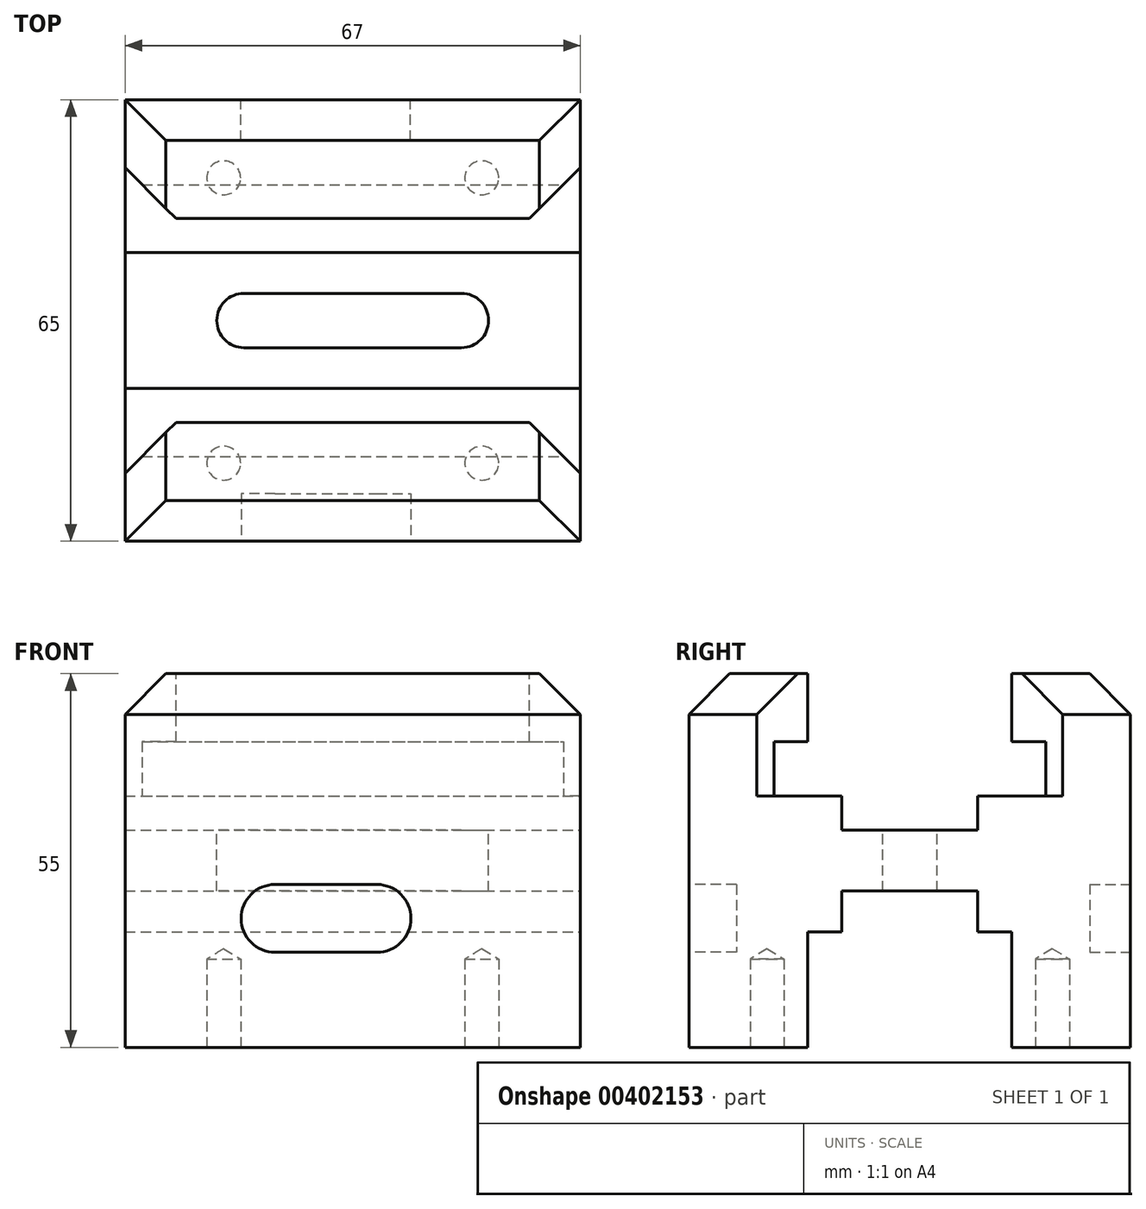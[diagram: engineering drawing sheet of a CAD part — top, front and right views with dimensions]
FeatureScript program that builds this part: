
annotation { "Feature Type Name" : "Feature", "Feature Type Description" : "" }
export const myFeature = defineFeature(function(context is Context, id is Id, definition is map)
    precondition{}
    {
        {
            var Q0;
            Q0=qCreatedBy(makeId("Front.planeOp"),FACE);
            var sketch = newSketch(context, id + "F0", { "sketchPlane" : qUnion([Q0])});
            skLineSegment(sketch, "E0.bottom", {"start": v(33.5, 27.5) * mm, "end": v(-33.5, 27.5) * mm});
            skLineSegment(sketch, "E0.top", {"start": v(33.5, -27.5) * mm, "end": v(-33.5, -27.5) * mm});
            skLineSegment(sketch, "E0.left", {"start": v(33.5, 27.5) * mm, "end": v(33.5, -27.5) * mm});
            skLineSegment(sketch, "E0.right", {"start": v(-33.5, 27.5) * mm, "end": v(-33.5, -27.5) * mm});
            skPoint(sketch, "E0.middle", {"position": v(0, 0) * mm});
            skSolve(sketch);
        }
        {
            var Q0;
            Q0=makeQuery(id+"F0.imprint","IMPRINT",FACE,{"disambiguationData":[TD([[makeQuery(id+"F0.imprint","IMPRINT",EDGE,{"derivedFrom":sQuery(id+"F0.wireOp",EDGE,"E0.bottom")}),1.0]])]});
            extrude(context, id + "F1", {"entities" : qUnion([Q0]), "depth" : 65 * mm, "symmetric" : true});
        }
        {
            var Q0;
            Q0=qCreatedBy(makeId("Right.planeOp"),FACE);
            var sketch = newSketch(context, id + "F2", { "sketchPlane" : qUnion([Q0])});
            skLineSegment(sketch, "E1", {"start": v(0, 0) * mm, "end": v(0, 27.5) * mm});
            skLineSegment(sketch, "E2", {"start": v(0, 27.5) * mm, "end": v(15, 27.5) * mm});
            skLineSegment(sketch, "E3", {"start": v(15, 27.5) * mm, "end": v(15, 17.5) * mm});
            skLineSegment(sketch, "E4", {"start": v(15, 17.5) * mm, "end": v(20, 17.5) * mm});
            skLineSegment(sketch, "E5", {"start": v(20, 17.5) * mm, "end": v(20, 9.5) * mm});
            skLineSegment(sketch, "E6", {"start": v(20, 9.5) * mm, "end": v(10, 9.5) * mm});
            skLineSegment(sketch, "E7", {"start": v(10, 9.5) * mm, "end": v(10, 4.5) * mm});
            skLineSegment(sketch, "E8", {"start": v(10, 4.5) * mm, "end": v(0, 4.5) * mm});
            skLineSegment(sketch, "E9.MirrorCS", {"start": v(-10, 9.5) * mm, "end": v(-10, 4.5) * mm});
            skLineSegment(sketch, "E10.MirrorCS", {"start": v(-20, 9.5) * mm, "end": v(-10, 9.5) * mm});
            skLineSegment(sketch, "E11.MirrorCS", {"start": v(-20, 17.5) * mm, "end": v(-20, 9.5) * mm});
            skLineSegment(sketch, "E12.MirrorCS", {"start": v(-10, 4.5) * mm, "end": v(0, 4.5) * mm});
            skLineSegment(sketch, "E13.MirrorCS", {"start": v(0, 27.5) * mm, "end": v(-15, 27.5) * mm});
            skLineSegment(sketch, "E14.MirrorCS", {"start": v(-15, 27.5) * mm, "end": v(-15, 17.5) * mm});
            skLineSegment(sketch, "E15.MirrorCS", {"start": v(-15, 17.5) * mm, "end": v(-20, 17.5) * mm});
            skLineSegment(sketch, "E16", {"start": v(0, 0) * mm, "end": v(0, -27.5) * mm});
            skLineSegment(sketch, "E17", {"start": v(0, -27.5) * mm, "end": v(15, -27.5) * mm});
            skLineSegment(sketch, "E18", {"start": v(15, -27.5) * mm, "end": v(15, -10.5) * mm});
            skLineSegment(sketch, "E19", {"start": v(15, -10.5) * mm, "end": v(10, -10.5) * mm});
            skLineSegment(sketch, "E20", {"start": v(10, -10.5) * mm, "end": v(10, -4.5) * mm});
            skLineSegment(sketch, "E21", {"start": v(10, -4.5) * mm, "end": v(0, -4.5) * mm});
            skLineSegment(sketch, "E22.MirrorCS", {"start": v(-10, -10.5) * mm, "end": v(-10, -4.5) * mm});
            skLineSegment(sketch, "E23.MirrorCS", {"start": v(-15, -27.5) * mm, "end": v(-15, -10.5) * mm});
            skLineSegment(sketch, "E24.MirrorCS", {"start": v(-10, -4.5) * mm, "end": v(0, -4.5) * mm});
            skLineSegment(sketch, "E25.MirrorCS", {"start": v(0, -27.5) * mm, "end": v(-15, -27.5) * mm});
            skLineSegment(sketch, "E26.MirrorCS", {"start": v(-15, -10.5) * mm, "end": v(-10, -10.5) * mm});
            skSolve(sketch);
        }
        {
            var Q0;
            Q0=makeQuery(id+"F2.imprint","IMPRINT",FACE,{"disambiguationData":[TD([[makeQuery(id+"F2.imprint","IMPRINT",EDGE,{"derivedFrom":sQuery(id+"F2.wireOp",EDGE,"E9.MirrorCS")}),1.0]])]});
            var Q1;
            {var subQ0=sQuery(id+"F2.wireOp",EDGE,"E2");Q1=makeQuery(id+"F2.imprint","IMPRINT",FACE,{"disambiguationData":[TD([[makeQuery(id+"F2.imprint","IMPRINT",EDGE,{"derivedFrom":subQ0}),-1.0]])]});}
            var Q2;
            {var subQ0=sQuery(id+"F2.wireOp",EDGE,"E17");Q2=makeQuery(id+"F2.imprint","IMPRINT",FACE,{"disambiguationData":[TD([[makeQuery(id+"F2.imprint","IMPRINT",EDGE,{"derivedFrom":subQ0}),1.0]])]});}
            var Q3;
            Q3=makeQuery(id+"F2.imprint","IMPRINT",FACE,{"disambiguationData":[TD([[makeQuery(id+"F2.imprint","IMPRINT",EDGE,{"derivedFrom":sQuery(id+"F2.wireOp",EDGE,"E22.MirrorCS")}),-1.0]])]});
            extrude(context, id + "F3", {"entities" : qUnion([Q0, Q1, Q2, Q3]), "operationType" : NewBodyOperationType.REMOVE, "oppositeDirection" : true, "depth" : 67 * mm, "symmetric" : true});
        }
        {
            var Q0;
            Q0=qCreatedBy(makeId("Top.planeOp"),FACE);
            var sketch = newSketch(context, id + "F4", { "sketchPlane" : qUnion([Q0])});
            skLineSegment(sketch, "E27.bottom", {"start": v(16, 4) * mm, "end": v(-16, 4) * mm});
            skLineSegment(sketch, "E27.top", {"start": v(16, -4) * mm, "end": v(-16, -4) * mm});
            skLineSegment(sketch, "E27.left", {"start": v(20, 0) * mm, "end": v(20, 0) * mm});
            skLineSegment(sketch, "E27.right", {"start": v(-20, 0) * mm, "end": v(-20, 0) * mm});
            skPoint(sketch, "E27.middle", {"position": v(0, 0) * mm});
            skPoint(sketch, "E28.visualSharp", {"position": v(20, -4) * mm});
            skArc(sketch, "E28.filletArc", {"start": v(16, -4) * mm, "mid": v(18.83, -2.83) * mm, "end": v(20, 0) * mm});
            skPoint(sketch, "E29.visualSharp", {"position": v(20, 4) * mm});
            skArc(sketch, "E29.filletArc", {"start": v(20, 0) * mm, "mid": v(18.83, 2.83) * mm, "end": v(16, 4) * mm});
            skPoint(sketch, "E30.visualSharp", {"position": v(-20, 4) * mm});
            skArc(sketch, "E30.filletArc", {"start": v(-16, 4) * mm, "mid": v(-18.83, 2.83) * mm, "end": v(-20, 0) * mm});
            skPoint(sketch, "E31.visualSharp", {"position": v(-20, -4) * mm});
            skArc(sketch, "E31.filletArc", {"start": v(-20, 0) * mm, "mid": v(-18.83, -2.83) * mm, "end": v(-16, -4) * mm});
            skSolve(sketch);
        }
        {
            var Q0;
            Q0=makeQuery(id+"F4.imprint","IMPRINT",FACE,{"disambiguationData":[TD([[makeQuery(id+"F4.imprint","IMPRINT",EDGE,{"derivedFrom":sQuery(id+"F4.wireOp",EDGE,"E27.bottom")}),1.0]])]});
            extrude(context, id + "F5", {"entities" : qUnion([Q0]), "operationType" : NewBodyOperationType.REMOVE, "oppositeDirection" : true, "depth" : (55 - 23 - 23) * mm, "symmetric" : true});
        }
        {
            var Q0;
            Q0=makeQuery(id+"F1.opExtrude","CAP_FACE",FACE,{"disambiguationData":[OSD([sQuery(id+"F0.wireOp",EDGE,"E0.bottom"),sQuery(id+"F0.wireOp",EDGE,"E0.top"),sQuery(id+"F0.wireOp",EDGE,"E0.left"),sQuery(id+"F0.wireOp",EDGE,"E0.right")])],"isStart":false});
            var sketch = newSketch(context, id + "F6", { "sketchPlane" : qUnion([Q0])});
            skLineSegment(sketch, "E32", {"start": v(0, 0) * mm, "end": v(0, -8.5) * mm});
            skPoint(sketch, "E32.endSnap0", {"position": v(0, -27.5) * mm});
            skLineSegment(sketch, "E33", {"start": v(0, -8.5) * mm, "end": v(-4, -8.5) * mm});
            skLineSegment(sketch, "E34.bottom", {"start": v(-11.43, -3.52) * mm, "end": v(3.57, -3.52) * mm});
            skLineSegment(sketch, "E34.top", {"start": v(-11.43, -13.52) * mm, "end": v(3.57, -13.52) * mm});
            skLineSegment(sketch, "E34.left", {"start": v(-16.43, -8.52) * mm, "end": v(-16.43, -8.52) * mm});
            skLineSegment(sketch, "E34.right", {"start": v(8.57, -8.52) * mm, "end": v(8.57, -8.52) * mm});
            skPoint(sketch, "E34.middle", {"position": v(-3.93, -8.52) * mm});
            skPoint(sketch, "E35.visualSharp", {"position": v(-16.43, -13.52) * mm});
            skArc(sketch, "E35.filletArc", {"start": v(-16.43, -8.52) * mm, "mid": v(-14.96, -12.06) * mm, "end": v(-11.43, -13.52) * mm});
            skPoint(sketch, "E36.visualSharp", {"position": v(-16.43, -3.52) * mm});
            skArc(sketch, "E36.filletArc", {"start": v(-11.43, -3.52) * mm, "mid": v(-14.96, -4.99) * mm, "end": v(-16.43, -8.52) * mm});
            skPoint(sketch, "E37.visualSharp", {"position": v(8.57, -3.52) * mm});
            skArc(sketch, "E37.filletArc", {"start": v(8.57, -8.52) * mm, "mid": v(7.1, -4.99) * mm, "end": v(3.57, -3.52) * mm});
            skPoint(sketch, "E38.visualSharp", {"position": v(8.57, -13.52) * mm});
            skArc(sketch, "E38.filletArc", {"start": v(3.57, -13.52) * mm, "mid": v(7.1, -12.06) * mm, "end": v(8.57, -8.52) * mm});
            skSolve(sketch);
        }
        {
            var Q0;
            Q0=makeQuery(id+"F1.opExtrude","CAP_FACE",FACE,{"disambiguationData":[OSD([sQuery(id+"F0.wireOp",EDGE,"E0.bottom"),sQuery(id+"F0.wireOp",EDGE,"E0.top"),sQuery(id+"F0.wireOp",EDGE,"E0.left"),sQuery(id+"F0.wireOp",EDGE,"E0.right")])],"isStart":true});
            var sketch = newSketch(context, id + "F7", { "sketchPlane" : qUnion([Q0])});
            skLineSegment(sketch, "E39", {"start": v(0, 0) * mm, "end": v(0, -8.5) * mm});
            skLineSegment(sketch, "E40", {"start": v(0, -8.5) * mm, "end": v(4, -8.5) * mm});
            skLineSegment(sketch, "E41.bottom", {"start": v(-3.5, -3.5) * mm, "end": v(11.5, -3.5) * mm});
            skLineSegment(sketch, "E41.top", {"start": v(-3.5, -13.5) * mm, "end": v(11.5, -13.5) * mm});
            skLineSegment(sketch, "E41.left", {"start": v(-8.5, -8.5) * mm, "end": v(-8.5, -8.5) * mm});
            skLineSegment(sketch, "E41.right", {"start": v(16.5, -8.5) * mm, "end": v(16.5, -8.5) * mm});
            skPoint(sketch, "E41.middle", {"position": v(4, -8.5) * mm});
            skPoint(sketch, "E42.visualSharp", {"position": v(-8.5, -3.5) * mm});
            skArc(sketch, "E42.filletArc", {"start": v(-3.5, -3.5) * mm, "mid": v(-7.04, -4.96) * mm, "end": v(-8.5, -8.5) * mm});
            skPoint(sketch, "E43.visualSharp", {"position": v(-8.5, -13.5) * mm});
            skArc(sketch, "E43.filletArc", {"start": v(-8.5, -8.5) * mm, "mid": v(-7.04, -12.04) * mm, "end": v(-3.5, -13.5) * mm});
            skPoint(sketch, "E44.visualSharp", {"position": v(16.5, -13.5) * mm});
            skArc(sketch, "E44.filletArc", {"start": v(11.5, -13.5) * mm, "mid": v(15.04, -12.04) * mm, "end": v(16.5, -8.5) * mm});
            skPoint(sketch, "E45.visualSharp", {"position": v(16.5, -3.5) * mm});
            skArc(sketch, "E45.filletArc", {"start": v(16.5, -8.5) * mm, "mid": v(15.04, -4.96) * mm, "end": v(11.5, -3.5) * mm});
            skSolve(sketch);
        }
        {
            var Q0;
            Q0=makeQuery(id+"F7.imprint","IMPRINT",FACE,{"disambiguationData":[TD([[makeQuery(id+"F7.imprint","IMPRINT",EDGE,{"derivedFrom":sQuery(id+"F7.wireOp",EDGE,"E41.top")}),1.0]])]});
            extrude(context, id + "F8", {"entities" : qUnion([Q0]), "operationType" : NewBodyOperationType.REMOVE, "oppositeDirection" : true, "depth" : 6 * mm});
        }
        {
            var Q0;
            Q0=makeQuery(id+"F6.imprint","IMPRINT",FACE,{"disambiguationData":[TD([[makeQuery(id+"F6.imprint","IMPRINT",EDGE,{"derivedFrom":sQuery(id+"F6.wireOp",EDGE,"E34.top")}),1.0]])]});
            extrude(context, id + "F9", {"entities" : qUnion([Q0]), "operationType" : NewBodyOperationType.REMOVE, "oppositeDirection" : true, "depth" : 7 * mm});
        }
        {
            var Q0;
            {var subQ2=sQuery(id+"F0.wireOp",EDGE,"E0.top");Q0=makeQuery(id+"F3.boolean.opBoolean","SPLIT",FACE,{"disambiguationData":[TD([makeQuery(id+"F3.opExtrude","SWEPT_FACE",FACE,{"disambiguationData":[OSD([sQuery(id+"F2.wireOp",EDGE,"E23.MirrorCS")])]})])],"derivedFrom":makeQuery(id+"F1.opExtrude","SWEPT_FACE",FACE,{"disambiguationData":[OSD([subQ2])]})});}
            var sketch = newSketch(context, id + "F10", { "sketchPlane" : qUnion([Q0])});
            skLineSegment(sketch, "E46.bottom", {"start": v(-19, 21) * mm, "end": v(19, 21) * mm});
            skLineSegment(sketch, "E46.top", {"start": v(-19, -21) * mm, "end": v(19, -21) * mm});
            skLineSegment(sketch, "E46.left", {"start": v(-19, 21) * mm, "end": v(-19, -21) * mm});
            skLineSegment(sketch, "E46.right", {"start": v(19, 21) * mm, "end": v(19, -21) * mm});
            skPoint(sketch, "E46.middle", {"position": v(0, 0) * mm});
            skCircle(sketch, "E47", {"center": v(-19, 21) * mm, "radius": 2.5 * mm});
            skCircle(sketch, "E48", {"center": v(19, 21) * mm, "radius": 2.5 * mm});
            skCircle(sketch, "E49", {"center": v(19, -21) * mm, "radius": 2.5 * mm});
            skCircle(sketch, "E50", {"center": v(-19, -21) * mm, "radius": 2.5 * mm});
            skSolve(sketch);
        }
        {
            var Q0;
            Q0=sQuery(id+"F10.wireOp",VERTEX,"E46.left.end");
            var Q1;
            Q1=sQuery(id+"F10.wireOp",VERTEX,"E47.center");
            var Q2;
            Q2=sQuery(id+"F10.wireOp",VERTEX,"E46.right.start");
            var Q3;
            Q3=sQuery(id+"F10.wireOp",VERTEX,"E46.right.end");
            var Q4;
            Q4=makeQuery(id+"F1.opExtrude","SWEPT_BODY",BODY,{"disambiguationData":[OSD([sQuery(id+"F0.wireOp",EDGE,"E0.bottom"),sQuery(id+"F0.wireOp",EDGE,"E0.top"),sQuery(id+"F0.wireOp",EDGE,"E0.left"),sQuery(id+"F0.wireOp",EDGE,"E0.right")])]});
            hole(context, id + "F11", {"style" : HoleStyle.SIMPLE, "endStyle" : HoleEndStyle.BLIND, "standardTappedOrClearance" : lookupTablePath({ "standard" : "ISO", "engagement" : "75%", "pitch" : "1 mm", "size" : "M6", "type" : "Tapped" }), "standardBlindInLast" : lookupTablePath({ "standard" : "ISO", "engagement" : "75%", "pitch" : "1 mm", "size" : "M6", "type" : "Tapped" }), "holeDiameter" : 5 * mm, "showTappedDepth" : true, "holeDepth" : 13 * mm, "isTappedThrough" : true, "tappedDepth" : 10 * mm, "tapClearance" : 3, "locations" : qUnion([Q0, Q1, Q2, Q3]), "scope" : qUnion([Q4]), "majorDiameter" : 6 * mm});
        }
        {
            var Q0;
            {var subQ2=sQuery(id+"F0.wireOp",EDGE,"E0.bottom");Q0=makeQuery(id+"F3.boolean.opBoolean","SPLIT",FACE,{"disambiguationData":[TD([makeQuery(id+"F3.opExtrude","SWEPT_FACE",FACE,{"disambiguationData":[OSD([sQuery(id+"F2.wireOp",EDGE,"E3")])]})])],"derivedFrom":makeQuery(id+"F1.opExtrude","SWEPT_FACE",FACE,{"disambiguationData":[OSD([subQ2])]})});}
            var sketch = newSketch(context, id + "F12", { "sketchPlane" : qUnion([Q0])});
            skLineSegment(sketch, "E51", {"start": v(0, 0) * mm, "end": v(0, 15) * mm});
            skLineSegment(sketch, "E52", {"start": v(0, 15) * mm, "end": v(-26, 15) * mm});
            skLineSegment(sketch, "E53", {"start": v(-33.5, 15) * mm, "end": v(-33.5, 22.5) * mm});
            skLineSegment(sketch, "E54", {"start": v(-33.5, 22.5) * mm, "end": v(-26, 15) * mm});
            skLineSegment(sketch, "E55", {"start": v(0, 0) * mm, "end": v(-39.07, 0) * mm});
            skLineSegment(sketch, "E56", {"start": v(0, 15) * mm, "end": v(0, 24.8) * mm});
            skLineSegment(sketch, "E57", {"start": v(-26, 15) * mm, "end": v(-33.5, 15) * mm});
            skLineSegment(sketch, "E58.MirrorCS", {"start": v(33.5, 22.5) * mm, "end": v(26, 15) * mm});
            skLineSegment(sketch, "E59.MirrorCS", {"start": v(33.5, 15) * mm, "end": v(33.5, 22.5) * mm});
            skLineSegment(sketch, "E60.MirrorCS", {"start": v(26, 15) * mm, "end": v(33.5, 15) * mm});
            skLineSegment(sketch, "E61.MirrorCS", {"start": v(33.5, -22.5) * mm, "end": v(26, -15) * mm});
            skLineSegment(sketch, "E62.MirrorCS", {"start": v(33.5, -15) * mm, "end": v(33.5, -22.5) * mm});
            skLineSegment(sketch, "E63.MirrorCS", {"start": v(26, -15) * mm, "end": v(33.5, -15) * mm});
            skLineSegment(sketch, "E64.MirrorCS", {"start": v(-33.5, -22.5) * mm, "end": v(-26, -15) * mm});
            skLineSegment(sketch, "E65.MirrorCS", {"start": v(0, -15) * mm, "end": v(-26, -15) * mm});
            skLineSegment(sketch, "E66.MirrorCS", {"start": v(-33.5, -15) * mm, "end": v(-33.5, -22.5) * mm});
            skLineSegment(sketch, "E67.MirrorCS", {"start": v(-26, -15) * mm, "end": v(-33.5, -15) * mm});
            skSolve(sketch);
        }
        {
            var Q0;
            Q0=makeQuery(id+"F12.imprint","IMPRINT",FACE,{"disambiguationData":[TD([[makeQuery(id+"F12.imprint","IMPRINT",EDGE,{"derivedFrom":sQuery(id+"F12.wireOp",EDGE,"E53")}),-1.0]])]});
            var Q1;
            Q1=makeQuery(id+"F12.imprint","IMPRINT",FACE,{"disambiguationData":[TD([[makeQuery(id+"F12.imprint","IMPRINT",EDGE,{"derivedFrom":sQuery(id+"F12.wireOp",EDGE,"E60.MirrorCS")}),1.0]])]});
            var Q2;
            Q2=makeQuery(id+"F12.imprint","IMPRINT",FACE,{"disambiguationData":[TD([[makeQuery(id+"F12.imprint","IMPRINT",EDGE,{"derivedFrom":sQuery(id+"F12.wireOp",EDGE,"E62.MirrorCS")}),-1.0]])]});
            var Q3;
            Q3=makeQuery(id+"F12.imprint","IMPRINT",FACE,{"disambiguationData":[TD([[makeQuery(id+"F12.imprint","IMPRINT",EDGE,{"derivedFrom":sQuery(id+"F12.wireOp",EDGE,"E64.MirrorCS")}),1.0]])]});
            extrude(context, id + "F13", {"entities" : qUnion([Q0, Q1, Q2, Q3]), "operationType" : NewBodyOperationType.REMOVE, "oppositeDirection" : true, "depth" : 18 * mm});
        }
        {
            var Q0;
            {var subQ0=sQuery(id+"F0.wireOp",EDGE,"E0.bottom");var subQ1=sQuery(id+"F0.wireOp",EDGE,"E0.left");Q0=makeQuery(id+"F3.boolean.opBoolean","SPLIT",EDGE,{"disambiguationData":[TD([makeQuery(id+"F3.opExtrude","SWEPT_FACE",FACE,{"disambiguationData":[OSD([sQuery(id+"F2.wireOp",EDGE,"E14.MirrorCS")])]})])],"derivedFrom":makeQuery(id+"F1.opExtrude","SWEPT_EDGE",EDGE,{"disambiguationData":[OSD([subQ0,subQ1])]})});}
            var Q1;
            Q1=makeQuery(id+"F1.opExtrude","CAP_EDGE",EDGE,{"disambiguationData":[OSD([sQuery(id+"F0.wireOp",EDGE,"E0.bottom")])],"isStart":false});
            var Q2;
            {var subQ0=sQuery(id+"F0.wireOp",EDGE,"E0.bottom");var subQ1=sQuery(id+"F0.wireOp",EDGE,"E0.right");Q2=makeQuery(id+"F3.boolean.opBoolean","SPLIT",EDGE,{"disambiguationData":[TD([makeQuery(id+"F3.opExtrude","SWEPT_FACE",FACE,{"disambiguationData":[OSD([sQuery(id+"F2.wireOp",EDGE,"E14.MirrorCS")])]})])],"derivedFrom":makeQuery(id+"F1.opExtrude","SWEPT_EDGE",EDGE,{"disambiguationData":[OSD([subQ0,subQ1])]})});}
            var Q3;
            {var subQ0=sQuery(id+"F0.wireOp",EDGE,"E0.bottom");var subQ1=sQuery(id+"F0.wireOp",EDGE,"E0.left");Q3=makeQuery(id+"F3.boolean.opBoolean","SPLIT",EDGE,{"disambiguationData":[TD([makeQuery(id+"F3.opExtrude","SWEPT_FACE",FACE,{"disambiguationData":[OSD([sQuery(id+"F2.wireOp",EDGE,"E3")])]})])],"derivedFrom":makeQuery(id+"F1.opExtrude","SWEPT_EDGE",EDGE,{"disambiguationData":[OSD([subQ0,subQ1])]})});}
            var Q4;
            Q4=makeQuery(id+"F1.opExtrude","CAP_EDGE",EDGE,{"disambiguationData":[OSD([sQuery(id+"F0.wireOp",EDGE,"E0.bottom")])],"isStart":true});
            var Q5;
            {var subQ0=sQuery(id+"F0.wireOp",EDGE,"E0.bottom");var subQ1=sQuery(id+"F0.wireOp",EDGE,"E0.right");Q5=makeQuery(id+"F3.boolean.opBoolean","SPLIT",EDGE,{"disambiguationData":[TD([makeQuery(id+"F3.opExtrude","SWEPT_FACE",FACE,{"disambiguationData":[OSD([sQuery(id+"F2.wireOp",EDGE,"E3")])]})])],"derivedFrom":makeQuery(id+"F1.opExtrude","SWEPT_EDGE",EDGE,{"disambiguationData":[OSD([subQ0,subQ1])]})});}
            chamfer(context, id + "F14", {"entities" : qUnion([Q0, Q1, Q2, Q3, Q4, Q5]), "width" : 6 * mm, "tangentPropagation" : true});
        }
    });
